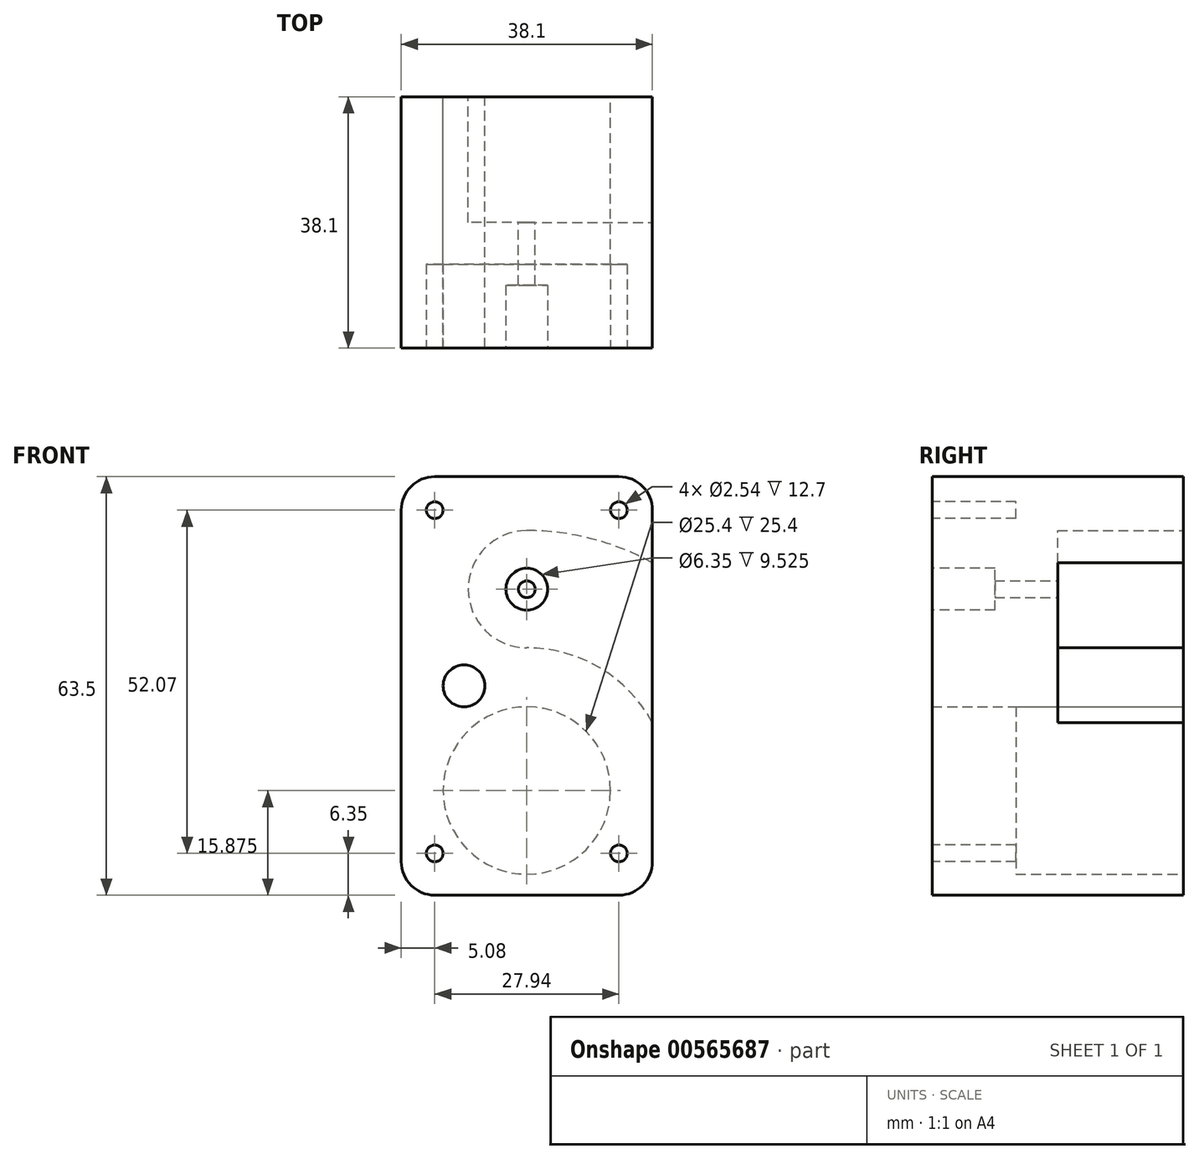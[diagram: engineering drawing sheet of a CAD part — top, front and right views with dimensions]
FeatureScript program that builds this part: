
annotation { "Feature Type Name" : "Feature", "Feature Type Description" : "" }
export const myFeature = defineFeature(function(context is Context, id is Id, definition is map)
    precondition{}
    {
        {
            var Q0;
            Q0=qCreatedBy(makeId("Front.planeOp"),FACE);
            var sketch = newSketch(context, id + "F0", { "sketchPlane" : qUnion([Q0])});
            skLineSegment(sketch, "E0.bottom", {"start": v(19.05, 31.75) * mm, "end": v(-19.05, 31.75) * mm});
            skLineSegment(sketch, "E0.top", {"start": v(19.05, -31.75) * mm, "end": v(-19.05, -31.75) * mm});
            skLineSegment(sketch, "E0.left", {"start": v(19.05, 31.75) * mm, "end": v(19.05, -31.75) * mm});
            skLineSegment(sketch, "E0.right", {"start": v(-19.05, 31.75) * mm, "end": v(-19.05, -31.75) * mm});
            skPoint(sketch, "E0.middle", {"position": v(0, 0) * mm});
            skLineSegment(sketch, "E1", {"start": v(0, 0) * mm, "end": v(-19.05, 0) * mm});
            skLineSegment(sketch, "E2", {"start": v(-19.05, 0) * mm, "end": v(-9.53, 0) * mm});
            skCircle(sketch, "E3", {"center": v(-9.53, 0) * mm, "radius": 3.18 * mm});
            skSolve(sketch);
        }
        {
            var Q0;
            Q0=makeQuery(id+"F0.imprint","IMPRINT",FACE,{"disambiguationData":[TD([[makeQuery(id+"F0.imprint","IMPRINT",EDGE,{"derivedFrom":sQuery(id+"F0.wireOp",EDGE,"E0.bottom")}),1.0]])]});
            var Q1;
            Q1 = qSketchRegion(id + "F2", true);
            extrude(context, id + "F1", {"entities" : qUnion([Q0, Q1]), "depth" : 38.1 * mm, "offsetDistance" : 25.4 * mm});
        }
        {
            var Q0;
            Q0=makeQuery(id+"F1.opExtrude","CAP_FACE",FACE,{"disambiguationData":[OSD([sQuery(id+"F0.wireOp",EDGE,"E0.bottom"),sQuery(id+"F0.wireOp",EDGE,"E0.top"),sQuery(id+"F0.wireOp",EDGE,"E0.left"),sQuery(id+"F0.wireOp",EDGE,"E0.right")])],"isStart":true});
            var sketch = newSketch(context, id + "F2", { "sketchPlane" : qUnion([Q0])});
            skLineSegment(sketch, "E4", {"start": v(0, 31.75) * mm, "end": v(0, 22.6) * mm});
            skPoint(sketch, "E4.endSnap0", {"position": v(0, 31.75) * mm});
            skLineSegment(sketch, "E5", {"start": v(0, 22.6) * mm, "end": v(0, 6.73) * mm});
            skCircle(sketch, "E6", {"center": v(0, 14.67) * mm, "radius": 8.9 * mm});
            skLineSegment(sketch, "E7", {"start": v(0, 6.73) * mm, "end": v(0, 0) * mm});
            skLineSegment(sketch, "E8", {"start": v(0, 0) * mm, "end": v(0, -3.17) * mm});
            skCircle(sketch, "E9", {"center": v(0, -15.88) * mm, "radius": 21.66 * mm});
            skCircle(sketch, "E10", {"center": v(0, -15.88) * mm, "radius": 39.44 * mm});
            skCircle(sketch, "E11", {"center": v(0, 14.67) * mm, "radius": 1.27 * mm});
            skLineSegment(sketch, "E12", {"start": v(19.05, 14.67) * mm, "end": v(-19.05, 14.67) * mm});
            skCircle(sketch, "E13", {"center": v(0, -15.88) * mm, "radius": 12.7 * mm});
            skLineSegment(sketch, "E14", {"start": v(0, -3.17) * mm, "end": v(0, 6.73) * mm});
            skLineSegment(sketch, "E15.trimOffspring", {"start": v(0, -28.58) * mm, "end": v(0, -31.75) * mm});
            skLineSegment(sketch, "E16", {"start": v(0, -15.88) * mm, "end": v(-39.44, -15.88) * mm});
            skSolve(sketch);
        }
        {
            var Q0;
            {var subQ3=sQuery(id+"F2.wireOp",EDGE,"E12");var subQ5=makeQuery(id+"F1.opExtrude","CAP_EDGE",EDGE,{"disambiguationData":[OSD([sQuery(id+"F0.wireOp",EDGE,"E0.left")])],"isStart":true});var subQ7=makeQuery(id+"F2.imprint","INTERSECT",VERTEX,{"derivedFrom":[subQ5,subQ3]});Q0=makeQuery(id+"F2.imprint","IMPRINT",FACE,{"disambiguationData":[TD([[makeQuery(id+"F2.imprint","IMPRINT",EDGE,{"disambiguationData":[TD([[subQ7,1.0]])],"derivedFrom":subQ3}),-1.0]])]});}
            var Q1;
            {var subQ0=sQuery(id+"F2.wireOp",EDGE,"E11");var subQ1=sQuery(id+"F2.wireOp",EDGE,"E5");var subQ2=makeQuery(id+"F2.imprint","INTERSECT",VERTEX,{"disambiguationData":[OD(0.0)],"derivedFrom":[subQ1,subQ0]});Q1=makeQuery(id+"F2.imprint","IMPRINT",FACE,{"disambiguationData":[TD([[makeQuery(id+"F2.imprint","IMPRINT",EDGE,{"disambiguationData":[TD([[subQ2,-1.0]])],"derivedFrom":subQ1}),1.0]])]});}
            var Q2;
            {var subQ0=sQuery(id+"F2.wireOp",EDGE,"E12");var subQ1=sQuery(id+"F2.wireOp",EDGE,"E5");var subQ2=makeQuery(id+"F2.imprint","INTERSECT",VERTEX,{"derivedFrom":[subQ1,subQ0]});Q2=makeQuery(id+"F2.imprint","IMPRINT",FACE,{"disambiguationData":[TD([[makeQuery(id+"F2.imprint","IMPRINT",EDGE,{"disambiguationData":[TD([[subQ2,-1.0]])],"derivedFrom":subQ1}),1.0]])]});}
            var Q3;
            {var subQ0=sQuery(id+"F2.wireOp",EDGE,"E11");var subQ1=sQuery(id+"F2.wireOp",EDGE,"E5");var subQ2=makeQuery(id+"F2.imprint","INTERSECT",VERTEX,{"disambiguationData":[OD(0.0)],"derivedFrom":[subQ1,subQ0]});Q3=makeQuery(id+"F2.imprint","IMPRINT",FACE,{"disambiguationData":[TD([[makeQuery(id+"F2.imprint","IMPRINT",EDGE,{"disambiguationData":[TD([[subQ2,-1.0]])],"derivedFrom":subQ1}),-1.0]])]});}
            var Q4;
            {var subQ0=sQuery(id+"F2.wireOp",EDGE,"E12");var subQ1=sQuery(id+"F2.wireOp",EDGE,"E5");var subQ2=makeQuery(id+"F2.imprint","INTERSECT",VERTEX,{"derivedFrom":[subQ1,subQ0]});Q4=makeQuery(id+"F2.imprint","IMPRINT",FACE,{"disambiguationData":[TD([[makeQuery(id+"F2.imprint","IMPRINT",EDGE,{"disambiguationData":[TD([[subQ2,-1.0]])],"derivedFrom":subQ1}),-1.0]])]});}
            var Q5;
            {var subQ3=sQuery(id+"F2.wireOp",EDGE,"E12");var subQ5=makeQuery(id+"F1.opExtrude","CAP_EDGE",EDGE,{"disambiguationData":[OSD([sQuery(id+"F0.wireOp",EDGE,"E0.left")])],"isStart":true});var subQ7=makeQuery(id+"F2.imprint","INTERSECT",VERTEX,{"derivedFrom":[subQ5,subQ3]});Q5=makeQuery(id+"F2.imprint","IMPRINT",FACE,{"disambiguationData":[TD([[makeQuery(id+"F2.imprint","IMPRINT",EDGE,{"disambiguationData":[TD([[subQ7,1.0]])],"derivedFrom":subQ3}),1.0]])]});}
            var Q6;
            {var subQ1=sQuery(id+"F2.wireOp",EDGE,"E5");var subQ3=sQuery(id+"F2.wireOp",EDGE,"E11");var subQ4=makeQuery(id+"F2.imprint","INTERSECT",VERTEX,{"disambiguationData":[OD(1.0)],"derivedFrom":[subQ1,subQ3]});Q6=makeQuery(id+"F2.imprint","IMPRINT",FACE,{"disambiguationData":[TD([[makeQuery(id+"F2.imprint","IMPRINT",EDGE,{"disambiguationData":[TD([[subQ4,1.0]])],"derivedFrom":subQ3}),-1.0]])]});}
            var Q7;
            {var subQ1=sQuery(id+"F2.wireOp",EDGE,"E5");var subQ3=sQuery(id+"F2.wireOp",EDGE,"E11");var subQ4=makeQuery(id+"F2.imprint","INTERSECT",VERTEX,{"disambiguationData":[OD(1.0)],"derivedFrom":[subQ1,subQ3]});Q7=makeQuery(id+"F2.imprint","IMPRINT",FACE,{"disambiguationData":[TD([[makeQuery(id+"F2.imprint","IMPRINT",EDGE,{"disambiguationData":[TD([[subQ4,-1.0]])],"derivedFrom":subQ3}),-1.0]])]});}
            var Q8;
            {var subQ1=sQuery(id+"F2.wireOp",EDGE,"E5");var subQ3=sQuery(id+"F2.wireOp",EDGE,"E11");var subQ4=makeQuery(id+"F2.imprint","INTERSECT",VERTEX,{"disambiguationData":[OD(0.0)],"derivedFrom":[subQ1,subQ3]});Q8=makeQuery(id+"F2.imprint","IMPRINT",FACE,{"disambiguationData":[TD([[makeQuery(id+"F2.imprint","IMPRINT",EDGE,{"disambiguationData":[TD([[subQ4,1.0]])],"derivedFrom":subQ3}),-1.0]])]});}
            var Q9;
            {var subQ1=sQuery(id+"F2.wireOp",EDGE,"E5");var subQ3=sQuery(id+"F2.wireOp",EDGE,"E11");var subQ4=makeQuery(id+"F2.imprint","INTERSECT",VERTEX,{"disambiguationData":[OD(0.0)],"derivedFrom":[subQ1,subQ3]});Q9=makeQuery(id+"F2.imprint","IMPRINT",FACE,{"disambiguationData":[TD([[makeQuery(id+"F2.imprint","IMPRINT",EDGE,{"disambiguationData":[TD([[subQ4,-1.0]])],"derivedFrom":subQ3}),-1.0]])]});}
            extrude(context, id + "F3", {"entities" : qUnion([Q0, Q1, Q2, Q3, Q4, Q5, Q6, Q7, Q8, Q9]), "operationType" : NewBodyOperationType.REMOVE, "oppositeDirection" : true, "depth" : 19.05 * mm, "offsetDistance" : 25.4 * mm});
        }
        {
            var Q0;
            {var subQ0=sQuery(id+"F2.wireOp",EDGE,"E11");var subQ1=sQuery(id+"F2.wireOp",EDGE,"E5");var subQ2=makeQuery(id+"F2.imprint","INTERSECT",VERTEX,{"disambiguationData":[OD(0.0)],"derivedFrom":[subQ1,subQ0]});Q0=makeQuery(id+"F2.imprint","IMPRINT",FACE,{"disambiguationData":[TD([[makeQuery(id+"F2.imprint","IMPRINT",EDGE,{"disambiguationData":[TD([[subQ2,-1.0]])],"derivedFrom":subQ1}),-1.0]])]});}
            var Q1;
            {var subQ0=sQuery(id+"F2.wireOp",EDGE,"E11");var subQ1=sQuery(id+"F2.wireOp",EDGE,"E5");var subQ2=makeQuery(id+"F2.imprint","INTERSECT",VERTEX,{"disambiguationData":[OD(0.0)],"derivedFrom":[subQ1,subQ0]});Q1=makeQuery(id+"F2.imprint","IMPRINT",FACE,{"disambiguationData":[TD([[makeQuery(id+"F2.imprint","IMPRINT",EDGE,{"disambiguationData":[TD([[subQ2,-1.0]])],"derivedFrom":subQ1}),1.0]])]});}
            var Q2;
            {var subQ0=sQuery(id+"F2.wireOp",EDGE,"E12");var subQ1=sQuery(id+"F2.wireOp",EDGE,"E5");var subQ2=makeQuery(id+"F2.imprint","INTERSECT",VERTEX,{"derivedFrom":[subQ1,subQ0]});Q2=makeQuery(id+"F2.imprint","IMPRINT",FACE,{"disambiguationData":[TD([[makeQuery(id+"F2.imprint","IMPRINT",EDGE,{"disambiguationData":[TD([[subQ2,-1.0]])],"derivedFrom":subQ1}),1.0]])]});}
            var Q3;
            {var subQ0=sQuery(id+"F2.wireOp",EDGE,"E12");var subQ1=sQuery(id+"F2.wireOp",EDGE,"E5");var subQ2=makeQuery(id+"F2.imprint","INTERSECT",VERTEX,{"derivedFrom":[subQ1,subQ0]});Q3=makeQuery(id+"F2.imprint","IMPRINT",FACE,{"disambiguationData":[TD([[makeQuery(id+"F2.imprint","IMPRINT",EDGE,{"disambiguationData":[TD([[subQ2,-1.0]])],"derivedFrom":subQ1}),-1.0]])]});}
            extrude(context, id + "F4", {"entities" : qUnion([Q0, Q1, Q2, Q3]), "operationType" : NewBodyOperationType.REMOVE, "oppositeDirection" : true, "depth" : 38.1 * mm, "offsetDistance" : 25.4 * mm});
        }
        {
            var Q0;
            {var subQ0=sQuery(id+"F2.wireOp",EDGE,"E13");var subQ1=makeQuery(id+"F2.imprint","INTERSECT",VERTEX,{"derivedFrom":[sQuery(id+"F2.wireOp",EDGE,"E14"),subQ0]});Q0=makeQuery(id+"F2.imprint","IMPRINT",FACE,{"disambiguationData":[TD([[makeQuery(id+"F2.imprint","IMPRINT",EDGE,{"disambiguationData":[TD([[subQ1,-1.0]])],"derivedFrom":subQ0}),1.0]])]});}
            extrude(context, id + "F5", {"entities" : qUnion([Q0]), "operationType" : NewBodyOperationType.REMOVE, "oppositeDirection" : true, "depth" : 25.4 * mm, "offsetDistance" : 25.4 * mm});
        }
        {
            var Q0;
            Q0=makeQuery(id+"F1.opExtrude","SWEPT_EDGE",EDGE,{"disambiguationData":[OSD([sQuery(id+"F0.wireOp",EDGE,"E0.bottom"),sQuery(id+"F0.wireOp",EDGE,"E0.left")])]});
            var Q1;
            Q1=makeQuery(id+"F1.opExtrude","SWEPT_EDGE",EDGE,{"disambiguationData":[OSD([sQuery(id+"F0.wireOp",EDGE,"E0.bottom"),sQuery(id+"F0.wireOp",EDGE,"E0.right")])]});
            fillet(context, id + "F6", {"entities" : qUnion([Q0, Q1]), "radius" : 5.08 * mm, "tangentPropagation" : true, "allowEdgeOverflow" : false});
        }
        {
            var Q0;
            Q0=makeQuery(id+"F1.opExtrude","CAP_FACE",FACE,{"disambiguationData":[OSD([sQuery(id+"F0.wireOp",EDGE,"E0.bottom"),sQuery(id+"F0.wireOp",EDGE,"E0.top"),sQuery(id+"F0.wireOp",EDGE,"E0.left"),sQuery(id+"F0.wireOp",EDGE,"E0.right"),sQuery(id+"F0.wireOp",EDGE,"E3")])],"isStart":false});
            var sketch = newSketch(context, id + "F7", { "sketchPlane" : qUnion([Q0])});
            skCircle(sketch, "E17", {"center": v(0, 14.67) * mm, "radius": 3.18 * mm});
            skLineSegment(sketch, "E18", {"start": v(-13.97, 26.67) * mm, "end": v(13.97, 26.67) * mm});
            skCircle(sketch, "E19", {"center": v(-13.97, 26.67) * mm, "radius": 1.27 * mm});
            skCircle(sketch, "E20", {"center": v(13.97, 26.67) * mm, "radius": 1.27 * mm});
            skLineSegment(sketch, "E21", {"start": v(-13.97, 26.67) * mm, "end": v(-13.97, -31.75) * mm});
            skLineSegment(sketch, "E22", {"start": v(13.97, 26.67) * mm, "end": v(13.97, -31.75) * mm});
            skLineSegment(sketch, "E23", {"start": v(-13.97, -31.75) * mm, "end": v(-13.97, -25.4) * mm});
            skLineSegment(sketch, "E24", {"start": v(-13.97, -25.4) * mm, "end": v(13.97, -25.4) * mm});
            skCircle(sketch, "E25", {"center": v(-13.97, -25.4) * mm, "radius": 1.27 * mm});
            skCircle(sketch, "E26", {"center": v(13.97, -25.4) * mm, "radius": 1.27 * mm});
            skSolve(sketch);
        }
        {
            var Q0;
            {var subQ0=sQuery(id+"F7.wireOp",EDGE,"E21");var subQ1=sQuery(id+"F7.wireOp",EDGE,"E18");var subQ2=makeQuery(id+"F7.imprint","INTERSECT",VERTEX,{"derivedFrom":[subQ1,subQ0]});Q0=makeQuery(id+"F7.imprint","IMPRINT",FACE,{"disambiguationData":[TD([[makeQuery(id+"F7.imprint","IMPRINT",EDGE,{"disambiguationData":[TD([[subQ2,-1.0]])],"derivedFrom":subQ1}),1.0]])]});}
            var Q1;
            {var subQ0=sQuery(id+"F7.wireOp",EDGE,"E21");var subQ1=sQuery(id+"F7.wireOp",EDGE,"E18");var subQ2=makeQuery(id+"F7.imprint","INTERSECT",VERTEX,{"derivedFrom":[subQ1,subQ0]});Q1=makeQuery(id+"F7.imprint","IMPRINT",FACE,{"disambiguationData":[TD([[makeQuery(id+"F7.imprint","IMPRINT",EDGE,{"disambiguationData":[TD([[subQ2,-1.0]])],"derivedFrom":subQ1}),-1.0]])]});}
            var Q2;
            {var subQ0=sQuery(id+"F7.wireOp",EDGE,"E22");var subQ1=sQuery(id+"F7.wireOp",EDGE,"E18");var subQ2=makeQuery(id+"F7.imprint","INTERSECT",VERTEX,{"derivedFrom":[subQ1,subQ0]});Q2=makeQuery(id+"F7.imprint","IMPRINT",FACE,{"disambiguationData":[TD([[makeQuery(id+"F7.imprint","IMPRINT",EDGE,{"disambiguationData":[TD([[subQ2,1.0]])],"derivedFrom":subQ1}),-1.0]])]});}
            var Q3;
            {var subQ0=sQuery(id+"F7.wireOp",EDGE,"E22");var subQ1=sQuery(id+"F7.wireOp",EDGE,"E18");var subQ2=makeQuery(id+"F7.imprint","INTERSECT",VERTEX,{"derivedFrom":[subQ1,subQ0]});Q3=makeQuery(id+"F7.imprint","IMPRINT",FACE,{"disambiguationData":[TD([[makeQuery(id+"F7.imprint","IMPRINT",EDGE,{"disambiguationData":[TD([[subQ2,1.0]])],"derivedFrom":subQ1}),1.0]])]});}
            var Q4;
            {var subQ1=sQuery(id+"F7.wireOp",EDGE,"E21");var subQ3=sQuery(id+"F7.wireOp",EDGE,"E25");var subQ4=makeQuery(id+"F7.imprint","INTERSECT",VERTEX,{"derivedFrom":[subQ1,subQ3]});Q4=makeQuery(id+"F7.imprint","IMPRINT",FACE,{"disambiguationData":[TD([[makeQuery(id+"F7.imprint","IMPRINT",EDGE,{"disambiguationData":[TD([[subQ4,-1.0]])],"derivedFrom":subQ3}),1.0]])]});}
            var Q5;
            {var subQ1=sQuery(id+"F7.wireOp",EDGE,"E21");var subQ3=sQuery(id+"F7.wireOp",EDGE,"E25");var subQ4=makeQuery(id+"F7.imprint","INTERSECT",VERTEX,{"derivedFrom":[subQ1,subQ3]});Q5=makeQuery(id+"F7.imprint","IMPRINT",FACE,{"disambiguationData":[TD([[makeQuery(id+"F7.imprint","IMPRINT",EDGE,{"disambiguationData":[TD([[subQ4,1.0]])],"derivedFrom":subQ3}),1.0]])]});}
            var Q6;
            {var subQ0=sQuery(id+"F7.wireOp",EDGE,"E22");var subQ1=makeQuery(id+"F7.imprint","INTERSECT",VERTEX,{"derivedFrom":[subQ0,sQuery(id+"F7.wireOp",EDGE,"E24")]});Q6=makeQuery(id+"F7.imprint","IMPRINT",FACE,{"disambiguationData":[TD([[makeQuery(id+"F7.imprint","IMPRINT",EDGE,{"disambiguationData":[TD([[subQ1,1.0]])],"derivedFrom":subQ0}),1.0]])]});}
            var Q7;
            {var subQ0=sQuery(id+"F7.wireOp",EDGE,"E24");var subQ1=sQuery(id+"F7.wireOp",EDGE,"E22");var subQ2=makeQuery(id+"F7.imprint","INTERSECT",VERTEX,{"derivedFrom":[subQ1,subQ0]});Q7=makeQuery(id+"F7.imprint","IMPRINT",FACE,{"disambiguationData":[TD([[makeQuery(id+"F7.imprint","IMPRINT",EDGE,{"disambiguationData":[TD([[subQ2,1.0]])],"derivedFrom":subQ1}),-1.0]])]});}
            var Q8;
            {var subQ0=sQuery(id+"F7.wireOp",EDGE,"E24");var subQ1=sQuery(id+"F7.wireOp",EDGE,"E22");var subQ2=makeQuery(id+"F7.imprint","INTERSECT",VERTEX,{"derivedFrom":[subQ1,subQ0]});Q8=makeQuery(id+"F7.imprint","IMPRINT",FACE,{"disambiguationData":[TD([[makeQuery(id+"F7.imprint","IMPRINT",EDGE,{"disambiguationData":[TD([[subQ2,-1.0]])],"derivedFrom":subQ1}),-1.0]])]});}
            var Q9;
            {var subQ1=sQuery(id+"F7.wireOp",EDGE,"E23");var subQ3=sQuery(id+"F7.wireOp",EDGE,"E25");var subQ4=makeQuery(id+"F7.imprint","INTERSECT",VERTEX,{"derivedFrom":[subQ1,subQ3]});Q9=makeQuery(id+"F7.imprint","IMPRINT",FACE,{"disambiguationData":[TD([[makeQuery(id+"F7.imprint","IMPRINT",EDGE,{"disambiguationData":[TD([[subQ4,-1.0]])],"derivedFrom":subQ3}),1.0]])]});}
            var Q10;
            Q10=makeQuery(id+"F7.imprint","IMPRINT",FACE,{"disambiguationData":[TD([[makeQuery(id+"F7.imprint","IMPRINT",EDGE,{"derivedFrom":sQuery(id+"F7.wireOp",EDGE,"E17")}),1.0]])]});
            extrude(context, id + "F8", {"entities" : qUnion([Q0, Q1, Q2, Q3, Q4, Q5, Q6, Q7, Q8, Q9, Q10]), "operationType" : NewBodyOperationType.REMOVE, "oppositeDirection" : true, "depth" : 9.52 * mm, "offsetDistance" : 25.4 * mm});
        }
        {
            var Q0;
            {var subQ0=sQuery(id+"F7.wireOp",EDGE,"E21");var subQ1=sQuery(id+"F7.wireOp",EDGE,"E18");var subQ2=makeQuery(id+"F7.imprint","INTERSECT",VERTEX,{"derivedFrom":[subQ1,subQ0]});Q0=makeQuery(id+"F7.imprint","IMPRINT",FACE,{"disambiguationData":[TD([[makeQuery(id+"F7.imprint","IMPRINT",EDGE,{"disambiguationData":[TD([[subQ2,-1.0]])],"derivedFrom":subQ1}),-1.0]])]});}
            var Q1;
            {var subQ0=sQuery(id+"F7.wireOp",EDGE,"E21");var subQ1=sQuery(id+"F7.wireOp",EDGE,"E18");var subQ2=makeQuery(id+"F7.imprint","INTERSECT",VERTEX,{"derivedFrom":[subQ1,subQ0]});Q1=makeQuery(id+"F7.imprint","IMPRINT",FACE,{"disambiguationData":[TD([[makeQuery(id+"F7.imprint","IMPRINT",EDGE,{"disambiguationData":[TD([[subQ2,-1.0]])],"derivedFrom":subQ1}),1.0]])]});}
            var Q2;
            {var subQ0=sQuery(id+"F7.wireOp",EDGE,"E22");var subQ1=sQuery(id+"F7.wireOp",EDGE,"E18");var subQ2=makeQuery(id+"F7.imprint","INTERSECT",VERTEX,{"derivedFrom":[subQ1,subQ0]});Q2=makeQuery(id+"F7.imprint","IMPRINT",FACE,{"disambiguationData":[TD([[makeQuery(id+"F7.imprint","IMPRINT",EDGE,{"disambiguationData":[TD([[subQ2,1.0]])],"derivedFrom":subQ1}),-1.0]])]});}
            var Q3;
            {var subQ0=sQuery(id+"F7.wireOp",EDGE,"E22");var subQ1=sQuery(id+"F7.wireOp",EDGE,"E18");var subQ2=makeQuery(id+"F7.imprint","INTERSECT",VERTEX,{"derivedFrom":[subQ1,subQ0]});Q3=makeQuery(id+"F7.imprint","IMPRINT",FACE,{"disambiguationData":[TD([[makeQuery(id+"F7.imprint","IMPRINT",EDGE,{"disambiguationData":[TD([[subQ2,1.0]])],"derivedFrom":subQ1}),1.0]])]});}
            var Q4;
            {var subQ0=sQuery(id+"F7.wireOp",EDGE,"E22");var subQ1=makeQuery(id+"F7.imprint","INTERSECT",VERTEX,{"derivedFrom":[subQ0,sQuery(id+"F7.wireOp",EDGE,"E24")]});Q4=makeQuery(id+"F7.imprint","IMPRINT",FACE,{"disambiguationData":[TD([[makeQuery(id+"F7.imprint","IMPRINT",EDGE,{"disambiguationData":[TD([[subQ1,1.0]])],"derivedFrom":subQ0}),1.0]])]});}
            var Q5;
            {var subQ0=sQuery(id+"F7.wireOp",EDGE,"E24");var subQ1=sQuery(id+"F7.wireOp",EDGE,"E22");var subQ2=makeQuery(id+"F7.imprint","INTERSECT",VERTEX,{"derivedFrom":[subQ1,subQ0]});Q5=makeQuery(id+"F7.imprint","IMPRINT",FACE,{"disambiguationData":[TD([[makeQuery(id+"F7.imprint","IMPRINT",EDGE,{"disambiguationData":[TD([[subQ2,1.0]])],"derivedFrom":subQ1}),-1.0]])]});}
            var Q6;
            {var subQ0=sQuery(id+"F7.wireOp",EDGE,"E24");var subQ1=sQuery(id+"F7.wireOp",EDGE,"E22");var subQ2=makeQuery(id+"F7.imprint","INTERSECT",VERTEX,{"derivedFrom":[subQ1,subQ0]});Q6=makeQuery(id+"F7.imprint","IMPRINT",FACE,{"disambiguationData":[TD([[makeQuery(id+"F7.imprint","IMPRINT",EDGE,{"disambiguationData":[TD([[subQ2,-1.0]])],"derivedFrom":subQ1}),-1.0]])]});}
            var Q7;
            {var subQ1=sQuery(id+"F7.wireOp",EDGE,"E23");var subQ3=sQuery(id+"F7.wireOp",EDGE,"E25");var subQ4=makeQuery(id+"F7.imprint","INTERSECT",VERTEX,{"derivedFrom":[subQ1,subQ3]});Q7=makeQuery(id+"F7.imprint","IMPRINT",FACE,{"disambiguationData":[TD([[makeQuery(id+"F7.imprint","IMPRINT",EDGE,{"disambiguationData":[TD([[subQ4,-1.0]])],"derivedFrom":subQ3}),1.0]])]});}
            var Q8;
            {var subQ1=sQuery(id+"F7.wireOp",EDGE,"E21");var subQ3=sQuery(id+"F7.wireOp",EDGE,"E25");var subQ4=makeQuery(id+"F7.imprint","INTERSECT",VERTEX,{"derivedFrom":[subQ1,subQ3]});Q8=makeQuery(id+"F7.imprint","IMPRINT",FACE,{"disambiguationData":[TD([[makeQuery(id+"F7.imprint","IMPRINT",EDGE,{"disambiguationData":[TD([[subQ4,1.0]])],"derivedFrom":subQ3}),1.0]])]});}
            var Q9;
            {var subQ1=sQuery(id+"F7.wireOp",EDGE,"E21");var subQ3=sQuery(id+"F7.wireOp",EDGE,"E25");var subQ4=makeQuery(id+"F7.imprint","INTERSECT",VERTEX,{"derivedFrom":[subQ1,subQ3]});Q9=makeQuery(id+"F7.imprint","IMPRINT",FACE,{"disambiguationData":[TD([[makeQuery(id+"F7.imprint","IMPRINT",EDGE,{"disambiguationData":[TD([[subQ4,-1.0]])],"derivedFrom":subQ3}),1.0]])]});}
            extrude(context, id + "F9", {"entities" : qUnion([Q0, Q1, Q2, Q3, Q4, Q5, Q6, Q7, Q8, Q9]), "operationType" : NewBodyOperationType.REMOVE, "oppositeDirection" : true, "depth" : 12.7 * mm, "offsetDistance" : 25.4 * mm});
        }
        {
            var Q0;
            Q0=makeQuery(id+"F1.opExtrude","SWEPT_EDGE",EDGE,{"disambiguationData":[OSD([sQuery(id+"F0.wireOp",EDGE,"E0.top"),sQuery(id+"F0.wireOp",EDGE,"E0.left")])]});
            var Q1;
            Q1=makeQuery(id+"F1.opExtrude","SWEPT_EDGE",EDGE,{"disambiguationData":[OSD([sQuery(id+"F0.wireOp",EDGE,"E0.top"),sQuery(id+"F0.wireOp",EDGE,"E0.right")])]});
            fillet(context, id + "F10", {"entities" : qUnion([Q0, Q1]), "radius" : 5.08 * mm, "tangentPropagation" : true, "allowEdgeOverflow" : false});
        }
    });
